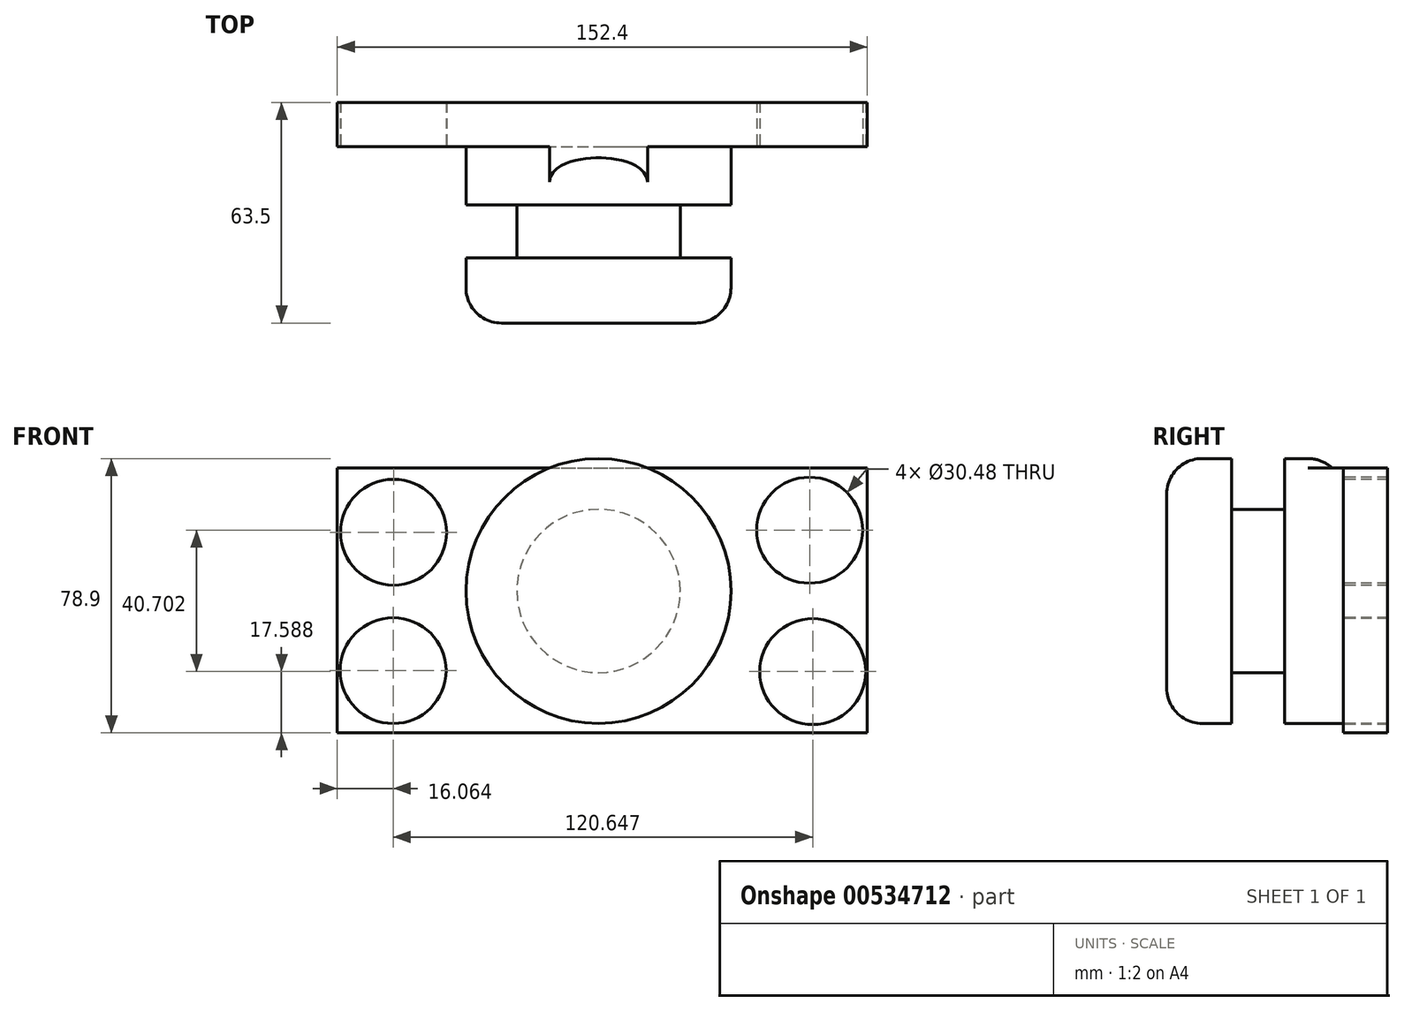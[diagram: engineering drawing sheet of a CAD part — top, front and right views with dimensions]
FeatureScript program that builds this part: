
annotation { "Feature Type Name" : "Feature", "Feature Type Description" : "" }
export const myFeature = defineFeature(function(context is Context, id is Id, definition is map)
    precondition{}
    {
        {
            var Q0;
            Q0=qCreatedBy(makeId("Front.planeOp"),FACE);
            var sketch = newSketch(context, id + "F0", { "sketchPlane" : qUnion([Q0])});
            skLineSegment(sketch, "E0.bottom", {"start": v(-75.1, 35.4) * mm, "end": v(77.3, 35.4) * mm});
            skLineSegment(sketch, "E0.top", {"start": v(-75.1, -40.8) * mm, "end": v(77.3, -40.8) * mm});
            skLineSegment(sketch, "E0.left", {"start": v(-75.1, 35.4) * mm, "end": v(-75.1, -40.8) * mm});
            skLineSegment(sketch, "E0.right", {"start": v(77.3, 35.4) * mm, "end": v(77.3, -40.8) * mm});
            skSolve(sketch);
        }
        {
            var Q0;
            Q0 = qSketchRegion(id + "F0", true);
            extrude(context, id + "F1", {"entities" : qUnion([Q0]), "depth" : 12.7 * mm, "offsetDistance" : 25.4 * mm});
        }
        {
            var Q0;
            Q0=makeQuery(id+"F1.opExtrude","CAP_FACE",FACE,{"disambiguationData":[OSD([sQuery(id+"F0.wireOp",EDGE,"E0.bottom"),sQuery(id+"F0.wireOp",EDGE,"E0.top"),sQuery(id+"F0.wireOp",EDGE,"E0.left"),sQuery(id+"F0.wireOp",EDGE,"E0.right")])],"isStart":false});
            var sketch = newSketch(context, id + "F2", { "sketchPlane" : qUnion([Q0])});
            skCircle(sketch, "E1", {"center": v(61.61, -23.21) * mm, "radius": 15.24 * mm});
            skCircle(sketch, "E2", {"center": v(60.71, 17.49) * mm, "radius": 15.24 * mm});
            skCircle(sketch, "E3", {"center": v(-59.04, -22.91) * mm, "radius": 15.24 * mm});
            skCircle(sketch, "E4", {"center": v(-58.92, 16.88) * mm, "radius": 15.24 * mm});
            skSolve(sketch);
        }
        {
            var Q0;
            Q0=makeQuery(id+"F2.imprint","IMPRINT",FACE,{"disambiguationData":[TD([[makeQuery(id+"F2.imprint","IMPRINT",EDGE,{"derivedFrom":sQuery(id+"F2.wireOp",EDGE,"E1")}),1.0]])]});
            var Q1;
            Q1=makeQuery(id+"F2.imprint","IMPRINT",FACE,{"disambiguationData":[TD([[makeQuery(id+"F2.imprint","IMPRINT",EDGE,{"derivedFrom":sQuery(id+"F2.wireOp",EDGE,"E2")}),1.0]])]});
            var Q2;
            Q2=makeQuery(id+"F2.imprint","IMPRINT",FACE,{"disambiguationData":[TD([[makeQuery(id+"F2.imprint","IMPRINT",EDGE,{"derivedFrom":sQuery(id+"F2.wireOp",EDGE,"E4")}),1.0]])]});
            var Q3;
            Q3=makeQuery(id+"F2.imprint","IMPRINT",FACE,{"disambiguationData":[TD([[makeQuery(id+"F2.imprint","IMPRINT",EDGE,{"derivedFrom":sQuery(id+"F2.wireOp",EDGE,"E3")}),1.0]])]});
            var Q4;
            Q4=sQuery(id+"F2.wireOp",EDGE,"E1");
            extrude(context, id + "F3", {"entities" : qUnion([Q0, Q1, Q2, Q3]), "operationType" : NewBodyOperationType.REMOVE, "surfaceEntities" : qUnion([Q4]), "endBound" : BoundingType.THROUGH_ALL, "oppositeDirection" : true, "depth" : 12.7 * mm, "offsetDistance" : 25.4 * mm});
        }
        {
            var Q0;
            Q0=qCreatedBy(makeId("Top.planeOp"),FACE);
            var sketch = newSketch(context, id + "F4", { "sketchPlane" : qUnion([Q0])});
            skLineSegment(sketch, "E5.bottom", {"start": v(-38.1, -63.5) * mm, "end": v(0, -63.5) * mm});
            skLineSegment(sketch, "E5.top", {"start": v(-38.1, -12.7) * mm, "end": v(0, -12.7) * mm});
            skLineSegment(sketch, "E5.left", {"start": v(-38.1, -63.5) * mm, "end": v(-38.1, -12.7) * mm});
            skLineSegment(sketch, "E5.right", {"start": v(0, -63.5) * mm, "end": v(0, -12.7) * mm});
            skSolve(sketch);
        }
        {
            var Q0;
            Q0 = qSketchRegion(id + "F4", true);
            var Q1;
            Q1=sQuery(id+"F4.wireOp",EDGE,"E5.right");
            revolve(context, id + "F5", {"operationType" : NewBodyOperationType.ADD, "entities" : qUnion([Q0]), "axis" : qUnion([Q1]), "revolveType" : RevolveType.FULL});
        }
        {
            var Q0;
            Q0=qCreatedBy(makeId("Top.planeOp"),FACE);
            var sketch = newSketch(context, id + "F6", { "sketchPlane" : qUnion([Q0])});
            skLineSegment(sketch, "E6.bottom", {"start": v(23.48, -44.8) * mm, "end": v(43.8, -44.8) * mm});
            skLineSegment(sketch, "E6.top", {"start": v(23.48, -29.55) * mm, "end": v(43.8, -29.55) * mm});
            skLineSegment(sketch, "E6.left", {"start": v(23.48, -44.8) * mm, "end": v(23.48, -29.55) * mm});
            skLineSegment(sketch, "E6.right", {"start": v(43.8, -44.8) * mm, "end": v(43.8, -29.55) * mm});
            skSolve(sketch);
        }
        {
            var Q0;
            Q0 = qSketchRegion(id + "F6", true);
            var Q1;
            Q1=makeQuery(id+"F5.opRevolve","SWEPT_FACE",FACE,{"disambiguationData":[OSD([sQuery(id+"F4.wireOp",EDGE,"E5.left")])]});
            revolve(context, id + "F7", {"operationType" : NewBodyOperationType.REMOVE, "entities" : qUnion([Q0]), "axis" : qUnion([Q1]), "revolveType" : RevolveType.FULL, "oppositeDirection" : true});
        }
        {
            var Q0;
            Q0=makeQuery(id+"F5.opRevolve","SWEPT_EDGE",EDGE,{"disambiguationData":[OSD([sQuery(id+"F4.wireOp",EDGE,"E5.bottom"),sQuery(id+"F4.wireOp",EDGE,"E5.left")])]});
            var Q1;
            {var subQ0=sQuery(id+"F4.wireOp",EDGE,"E5.left");Q1=makeQuery(id+"F5.boolean.opBoolean","SPLIT",EDGE,{"disambiguationData":[topologyDisambiguationEdgeConnected([makeQuery(id+"F1.opExtrude","CAP_FACE",FACE,{"disambiguationData":[OSD([sQuery(id+"F0.wireOp",EDGE,"E0.bottom"),sQuery(id+"F0.wireOp",EDGE,"E0.top"),sQuery(id+"F0.wireOp",EDGE,"E0.left"),sQuery(id+"F0.wireOp",EDGE,"E0.right")])],"isStart":false})])],"derivedFrom":makeQuery(id+"F5.opRevolve","SWEPT_EDGE",EDGE,{"disambiguationData":[OSD([sQuery(id+"F4.wireOp",EDGE,"E5.top"),subQ0])]})});}
            fillet(context, id + "F8", {"entities" : qUnion([Q0, Q1]), "radius" : 10.16 * mm, "tangentPropagation" : true, "allowEdgeOverflow" : false});
        }
    });
